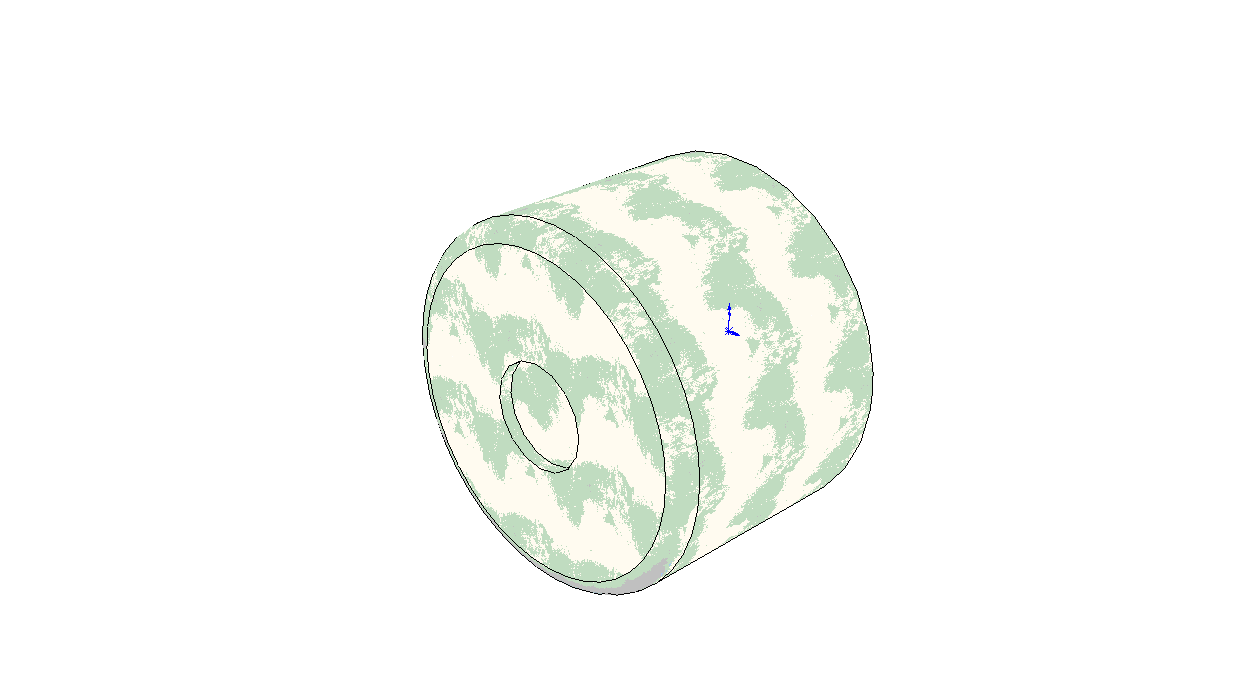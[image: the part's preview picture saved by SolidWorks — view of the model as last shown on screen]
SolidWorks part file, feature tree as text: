
SOLIDWORKS PART (.sldprt)
format: sldprt  version: not decoded by parser v0  size: 137,216 bytes
history: native  units: mm
features: plane x3, sketch x2, material x1, extrude x1, fillet x1, shell x1, cut_extrude x1 (+8 scaffold rows collapsed)
feature tree (18):
  scaffold x8  (default folders/planes/origin — collapsed)
  material  "Matériau <non spécifié>"
  plane  "Plan de face"
  plane  "Plan de dessus"
  plane  "Plan de droite"
  sketch  "Esquisse1"  dims[D1=~20.114168mm]
  extrude  "Extrusion1"  Depth=18.7mm
  fillet  "Congé1"  Radius=1.5mm
  shell  "Coque1"  Thickness=1mm
  sketch  "Esquisse2"  dims[D1=~1.93524mm]
  cut_extrude  "Enlèv. mat.-Extru.1"  [1 undecoded]
decode coverage: 5 of 6 modeling features carry decoded parameters
note: ~ marks probable driven/reference dimensions
note: 1 parameter value undecoded
note: suppression state not decoded; provenance and decode notes live in map.json
